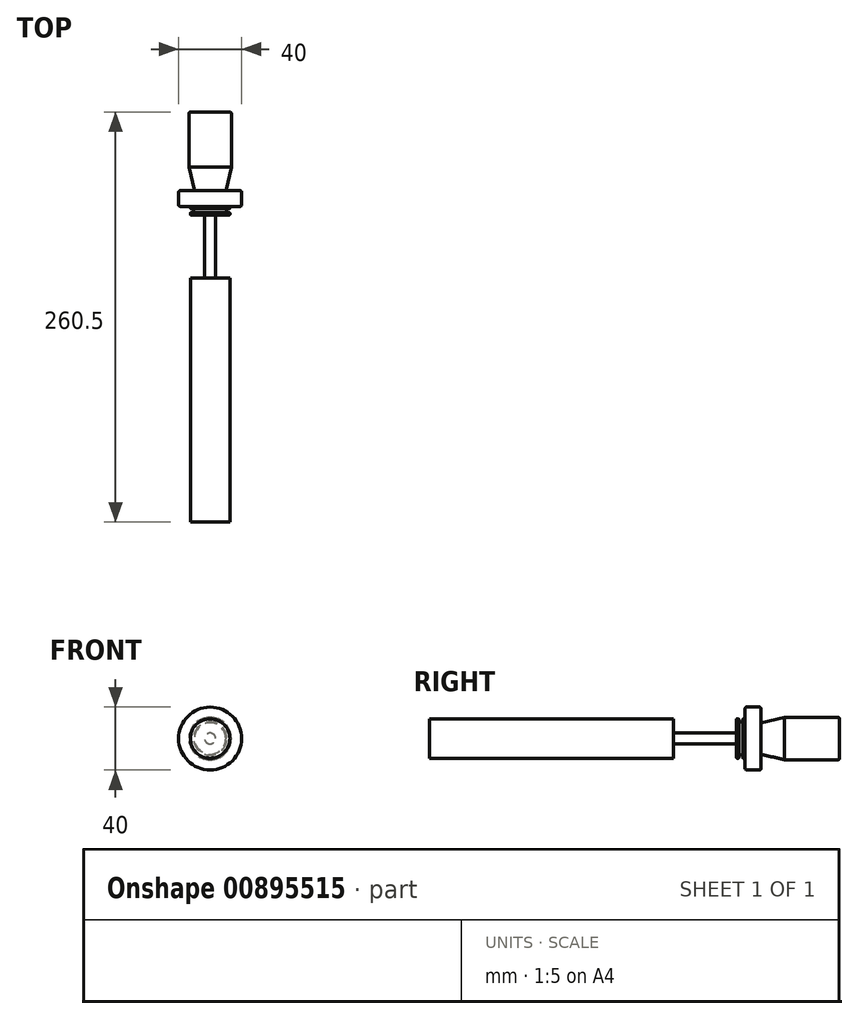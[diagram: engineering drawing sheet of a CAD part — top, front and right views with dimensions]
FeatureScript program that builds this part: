
annotation { "Feature Type Name" : "Feature", "Feature Type Description" : "" }
export const myFeature = defineFeature(function(context is Context, id is Id, definition is map)
    precondition{}
    {
        {
            var Q0;
            Q0=qCreatedBy(makeId("Top.planeOp"),FACE);
            var sketch = newSketch(context, id + "F0", { "sketchPlane" : qUnion([Q0])});
            skLineSegment(sketch, "E0", {"start": v(-16.18, -69.76) * mm, "end": v(8.82, -69.76) * mm});
            skLineSegment(sketch, "E1", {"start": v(8.82, -69.76) * mm, "end": v(8.82, 85.24) * mm});
            skLineSegment(sketch, "E2", {"start": v(8.82, 85.24) * mm, "end": v(-0.18, 85.24) * mm});
            skLineSegment(sketch, "E3", {"start": v(-0.18, 85.24) * mm, "end": v(-0.18, 130.74) * mm});
            skLineSegment(sketch, "E4", {"start": v(-0.18, 130.74) * mm, "end": v(16.32, 130.74) * mm});
            skLineSegment(sketch, "E5", {"start": v(16.32, 130.74) * mm, "end": v(16.32, 140.74) * mm});
            skLineSegment(sketch, "E6", {"start": v(-23.68, 140.74) * mm, "end": v(-23.68, 130.74) * mm});
            skLineSegment(sketch, "E7", {"start": v(-23.68, 130.74) * mm, "end": v(-7.18, 130.74) * mm});
            skLineSegment(sketch, "E8", {"start": v(-7.18, 130.74) * mm, "end": v(-7.18, 85.24) * mm});
            skLineSegment(sketch, "E9", {"start": v(-7.18, 85.24) * mm, "end": v(-16.18, 85.24) * mm});
            skLineSegment(sketch, "E10", {"start": v(-16.18, 85.24) * mm, "end": v(-16.18, -69.76) * mm});
            skLineSegment(sketch, "E11", {"start": v(-3.68, -69.76) * mm, "end": v(-3.68, 190.74) * mm});
            skLineSegment(sketch, "E12", {"start": v(9.82, 190.74) * mm, "end": v(-17.18, 190.74) * mm});
            skLineSegment(sketch, "E13", {"start": v(-0.18, 125.24) * mm, "end": v(8.87, 125.24) * mm});
            skLineSegment(sketch, "E14", {"start": v(8.87, 125.24) * mm, "end": v(8.87, 126.74) * mm});
            skLineSegment(sketch, "E15", {"start": v(8.87, 126.74) * mm, "end": v(6.87, 126.74) * mm});
            skLineSegment(sketch, "E16", {"start": v(6.87, 126.74) * mm, "end": v(6.87, 129.24) * mm});
            skLineSegment(sketch, "E17", {"start": v(6.87, 129.24) * mm, "end": v(8.87, 129.24) * mm});
            skLineSegment(sketch, "E18", {"start": v(8.87, 129.24) * mm, "end": v(8.87, 130.74) * mm});
            skLineSegment(sketch, "E19", {"start": v(6.32, 140.74) * mm, "end": v(16.32, 140.74) * mm});
            skLineSegment(sketch, "E20", {"start": v(-13.68, 140.74) * mm, "end": v(-23.68, 140.74) * mm});
            skLineSegment(sketch, "E21", {"start": v(6.32, 140.74) * mm, "end": v(9.82, 155.74) * mm});
            skLineSegment(sketch, "E22", {"start": v(9.82, 155.74) * mm, "end": v(9.82, 190.74) * mm});
            skLineSegment(sketch, "E23", {"start": v(-17.18, 190.74) * mm, "end": v(-17.18, 155.74) * mm});
            skLineSegment(sketch, "E24", {"start": v(-17.18, 155.74) * mm, "end": v(-13.68, 140.74) * mm});
            skSolve(sketch);
        }
        {
            var Q0;
            {var subQ0=sQuery(id+"F0.wireOp",EDGE,"E1");Q0=makeQuery(id+"F0.imprint","IMPRINT",FACE,{"disambiguationData":[TD([[makeQuery(id+"F0.imprint","IMPRINT",EDGE,{"derivedFrom":subQ0}),1.0]])]});}
            var Q1;
            {var subQ0=sQuery(id+"F0.wireOp",EDGE,"E13");Q1=makeQuery(id+"F0.imprint","IMPRINT",FACE,{"disambiguationData":[TD([[makeQuery(id+"F0.imprint","IMPRINT",EDGE,{"derivedFrom":subQ0}),1.0]])]});}
            var Q2;
            Q2=sQuery(id+"F0.wireOp",EDGE,"E11");
            revolve(context, id + "F1", {"surfaceOperationType" : NewSurfaceOperationType.NEW, "entities" : qUnion([Q0, Q1]), "axis" : qUnion([Q2]), "revolveType" : RevolveType.FULL});
        }
        {
            var Q0;
            Q0=makeQuery(id+"F1.opRevolve","SWEPT_EDGE",EDGE,{"disambiguationData":[OSD([sQuery(id+"F0.wireOp",EDGE,"E12"),sQuery(id+"F0.wireOp",EDGE,"E22")])]});
            var Q1;
            Q1=makeQuery(id+"F1.opRevolve","SWEPT_EDGE",EDGE,{"disambiguationData":[OSD([sQuery(id+"F0.wireOp",EDGE,"E5"),sQuery(id+"F0.wireOp",EDGE,"E19")])]});
            var Q2;
            Q2=makeQuery(id+"F1.opRevolve","SWEPT_EDGE",EDGE,{"disambiguationData":[OSD([sQuery(id+"F0.wireOp",EDGE,"E4"),sQuery(id+"F0.wireOp",EDGE,"E5")])]});
            fillet(context, id + "F2", {"entities" : qUnion([Q0, Q1, Q2]), "radius" : 1 * mm, "tangentPropagation" : true, "allowEdgeOverflow" : false});
        }
        {
            var Q0;
            Q0=makeQuery(id+"F1.opRevolve","SWEPT_EDGE",EDGE,{"disambiguationData":[OSD([sQuery(id+"F0.wireOp",EDGE,"E13"),sQuery(id+"F0.wireOp",EDGE,"E14")])]});
            var Q1;
            Q1=makeQuery(id+"F1.opRevolve","SWEPT_EDGE",EDGE,{"disambiguationData":[OSD([sQuery(id+"F0.wireOp",EDGE,"E14"),sQuery(id+"F0.wireOp",EDGE,"E15")])]});
            var Q2;
            Q2=makeQuery(id+"F1.opRevolve","SWEPT_EDGE",EDGE,{"disambiguationData":[OSD([sQuery(id+"F0.wireOp",EDGE,"E17"),sQuery(id+"F0.wireOp",EDGE,"E18")])]});
            fillet(context, id + "F3", {"entities" : qUnion([Q0, Q1, Q2]), "radius" : 0.5 * mm, "tangentPropagation" : true, "allowEdgeOverflow" : false});
        }
    });
